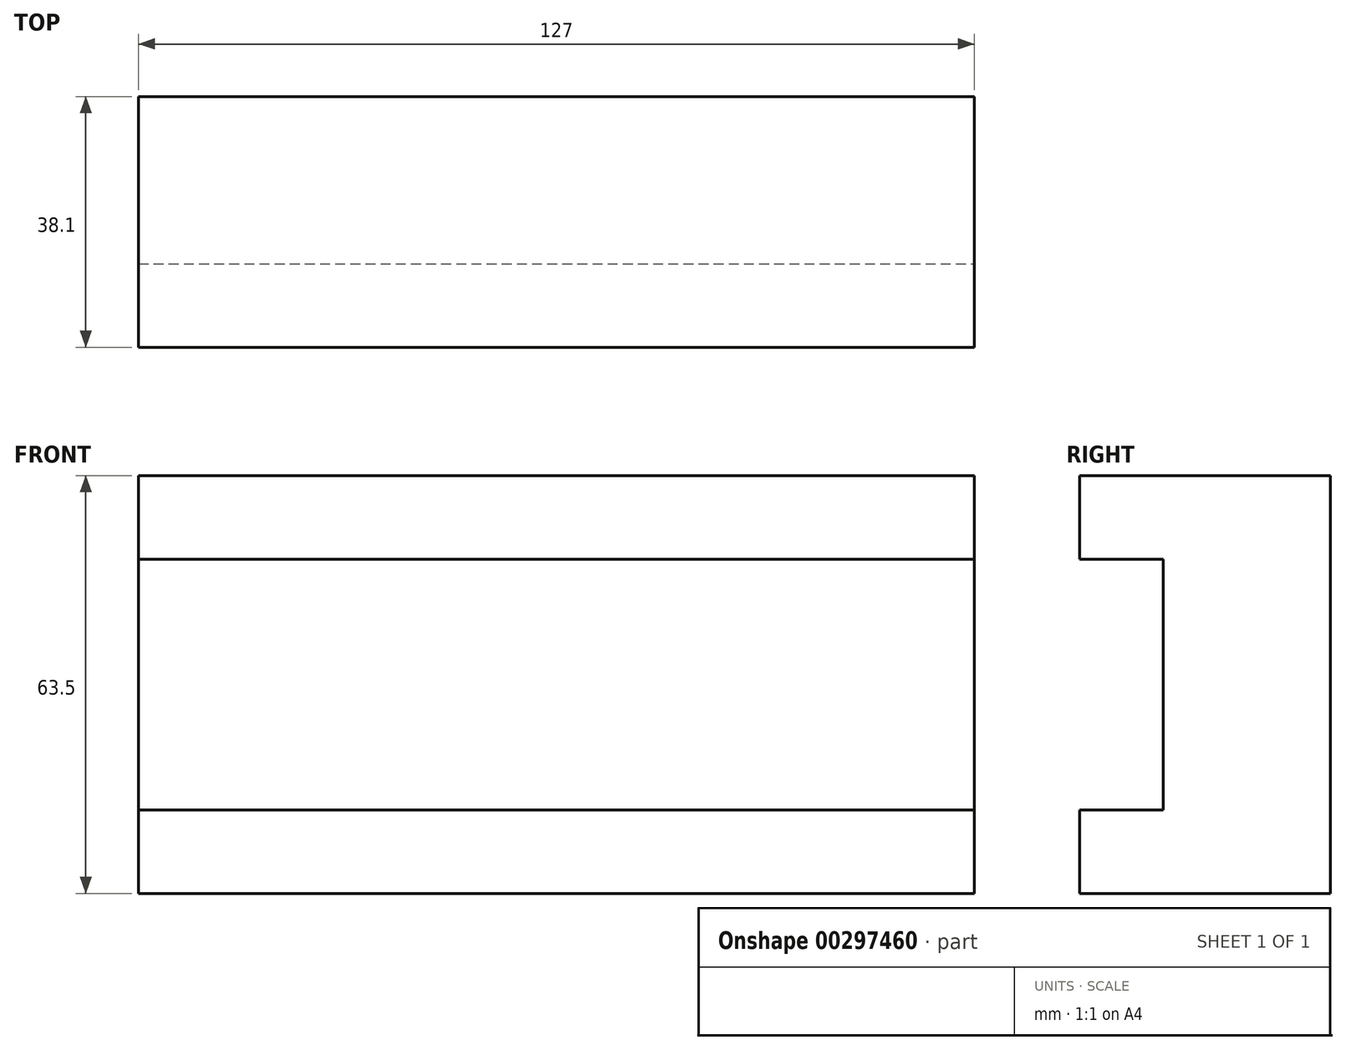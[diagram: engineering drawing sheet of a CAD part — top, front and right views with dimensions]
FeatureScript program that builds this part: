
annotation { "Feature Type Name" : "Feature", "Feature Type Description" : "" }
export const myFeature = defineFeature(function(context is Context, id is Id, definition is map)
    precondition{}
    {
        {
            var Q0;
            Q0=qCreatedBy(makeId("Front.planeOp"),FACE);
            var sketch = newSketch(context, id + "F0", { "sketchPlane" : qUnion([Q0])});
            skLineSegment(sketch, "E0.bottom", {"start": v(63.5, 31.75) * mm, "end": v(-63.5, 31.75) * mm});
            skLineSegment(sketch, "E0.top", {"start": v(63.5, -31.75) * mm, "end": v(-63.5, -31.75) * mm});
            skLineSegment(sketch, "E0.left", {"start": v(63.5, 31.75) * mm, "end": v(63.5, -31.75) * mm});
            skLineSegment(sketch, "E0.right", {"start": v(-63.5, 31.75) * mm, "end": v(-63.5, -31.75) * mm});
            skPoint(sketch, "E0.middle", {"position": v(0, 0) * mm});
            skSolve(sketch);
        }
        {
            var Q0;
            Q0 = qSketchRegion(id + "F0", true);
            extrude(context, id + "F1", {"entities" : qUnion([Q0]), "depth" : 38.1 * mm});
        }
        {
            var Q0;
            Q0=makeQuery(id+"F1.opExtrude","CAP_FACE",FACE,{"disambiguationData":[OSD([sQuery(id+"F0.wireOp",EDGE,"E0.bottom"),sQuery(id+"F0.wireOp",EDGE,"E0.top"),sQuery(id+"F0.wireOp",EDGE,"E0.left"),sQuery(id+"F0.wireOp",EDGE,"E0.right")])],"isStart":false});
            var sketch = newSketch(context, id + "F2", { "sketchPlane" : qUnion([Q0])});
            skLineSegment(sketch, "E1.bottom", {"start": v(-63.5, 19.05) * mm, "end": v(63.5, 19.05) * mm});
            skLineSegment(sketch, "E1.top", {"start": v(-63.5, -19.05) * mm, "end": v(63.5, -19.05) * mm});
            skLineSegment(sketch, "E1.left", {"start": v(-63.5, 19.05) * mm, "end": v(-63.5, -19.05) * mm});
            skLineSegment(sketch, "E1.right", {"start": v(63.5, 19.05) * mm, "end": v(63.5, -19.05) * mm});
            skSolve(sketch);
        }
        {
            var Q0;
            Q0=makeQuery(id+"F2.imprint","IMPRINT",FACE,{"disambiguationData":[TD([[makeQuery(id+"F2.imprint","IMPRINT",EDGE,{"derivedFrom":sQuery(id+"F2.wireOp",EDGE,"E1.bottom")}),-1.0]])]});
            extrude(context, id + "F3", {"entities" : qUnion([Q0]), "operationType" : NewBodyOperationType.REMOVE, "oppositeDirection" : true, "depth" : 12.7 * mm});
        }
    });
